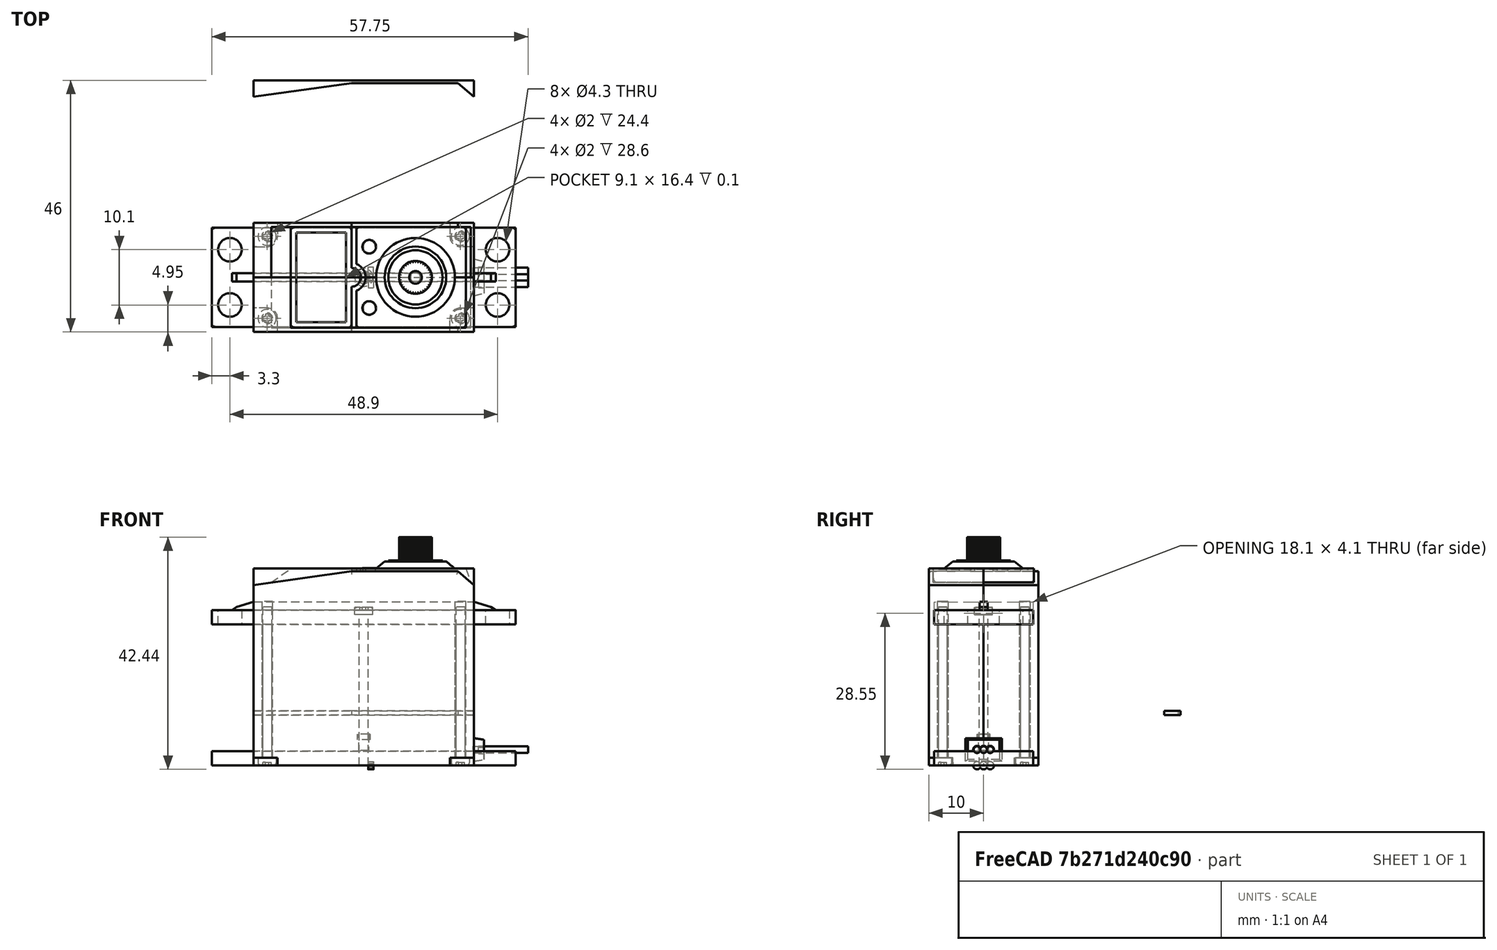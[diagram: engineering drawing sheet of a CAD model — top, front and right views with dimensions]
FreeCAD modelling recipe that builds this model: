
FCSTD DOCUMENT  (FreeCAD 0.14R3702 (Git))
Label: Futaba3003
Comment: It has been modeled using a caliper and a real Futaba 3003 servo
License: CC-BY 3.0
LicenseURL: http://creativecommons.org/licenses/by/3.0/
objects: Sketcher::SketchObject×24, PartDesign::Pocket×12, Part::Feature×10, Part::MultiFuse×7, App::DocumentObjectGroup×6, PartDesign::Pad×5, Part::Loft×3, Part::Cylinder×3, Part::Mirroring×2, Part::Fillet×2, PartDesign::PolarPattern×1, PartDesign::Revolution×1, PartDesign::Fillet×1, PartDesign::Mirrored×1, Part::Cut×1
note: 91 computed .brp shape members not serialized (recipe doc carries the construction recipe); baked Part::Feature solids carry a one-line shape summary decoded from their .brp

FEATURE [Sketcher::SketchObject] Sketch  label="body-sketch"
  Placement = pos=(0,0,0) rot=(1,0,0;1.5708rad)
  sketch-geometry (4):
    g0: LineSegment StartX=-20.15 StartY=36 StartZ=0 EndX=20.15 EndY=36 EndZ=0
    g1: LineSegment StartX=20.15 StartY=0 StartZ=0 EndX=-20.15 EndY=0 EndZ=0
    g2: LineSegment StartX=-20.15 StartY=0 StartZ=0 EndX=-20.15 EndY=36 EndZ=0
    g3: LineSegment StartX=20.15 StartY=36 StartZ=0 EndX=20.15 EndY=0 EndZ=0
  constraints (11):
    c: Coincident(g3,g1)
    c: Coincident(g1,g2)
    c: Horizontal(g0)
    c: Horizontal(g1)
    c: Vertical(g2)
    c: Symmetric(g0,g0,g-2)
    c: PointOnObject(g3,g-1)
    c: DistanceX(g0) = 40.3
    c: DistanceY(g0,g1) = -36
    c: Coincident(g2,g0)
    c: Coincident(g3,g0)
FEATURE [PartDesign::Pad] Pad  label="main_body"
  Length = 10
  Length2 = 100
  Placement = pos=(0,0,0) rot=(1,0,0;1.5708rad)
  Sketch = -> Sketch
  Type = 0
FEATURE [Sketcher::SketchObject] Sketch001  label="lateral-layer1-sketch"
  ExternalGeometry = -> [Pad]
  Placement = pos=(0,-10,0) rot=(1,0,0;1.5708rad)
  Support = -> Pad [Face14]
  sketch-geometry (6):
    g0: LineSegment StartX=20.15 StartY=33 StartZ=0 EndX=17.18 EndY=35.52 EndZ=0
    g1: LineSegment StartX=17.18 StartY=35.52 StartZ=0 EndX=-2.25 EndY=35.52 EndZ=0
    g2: LineSegment StartX=-2.25 StartY=35.52 StartZ=0 EndX=-20.15 EndY=33 EndZ=0
    g3: LineSegment StartX=-20.15 StartY=33 StartZ=0 EndX=-20.15 EndY=36 EndZ=0
    g4: LineSegment StartX=-20.15 StartY=36 StartZ=0 EndX=20.15 EndY=36 EndZ=0
    g5: LineSegment StartX=20.15 StartY=36 StartZ=0 EndX=20.15 EndY=33 EndZ=0
  constraints (16):
    c: Coincident(g0,g1)
    c: Horizontal(g1)
    c: Coincident(g1,g2)
    c: Coincident(g3,g2)
    c: Coincident(g4,g3)
    c: DistanceY(g0) = 33
    c: DistanceY(g4,g0) = -0.48
    c: DistanceX(g0,g0) = -2.97
    c: DistanceX(g4,g1) = -22.4
    c: Coincident(g5,g4)
    c: Coincident(g5,g0)
    c: PointOnObject(g0,g-4)
    c: Coincident(g4,g-4)
    c: Coincident(g3,g-3)
    c: PointOnObject(g2,g-3)
    c: DistanceY(g-1,g2) = 33
FEATURE [Sketcher::SketchObject] Sketch003
  Placement = pos=(0,0,0) rot=(0.57735,0.57735,0.57735;2.0944rad)
  sketch-geometry (4):
    g0: LineSegment StartX=-3.35 StartY=2.1 StartZ=0 EndX=3.35 EndY=2.1 EndZ=0
    g1: LineSegment StartX=3.35 StartY=2.1 StartZ=0 EndX=3.35 EndY=-2.1 EndZ=0
    g2: LineSegment StartX=3.35 StartY=-2.1 StartZ=0 EndX=-3.35 EndY=-2.1 EndZ=0
    g3: LineSegment StartX=-3.35 StartY=-2.1 StartZ=0 EndX=-3.35 EndY=2.1 EndZ=0
  constraints (12):
    c: Coincident(g0,g1)
    c: Coincident(g2,g3)
    c: Coincident(g3,g0)
    c: Horizontal(g0)
    c: Horizontal(g2)
    c: Vertical(g1)
    c: Vertical(g3)
    c: Symmetric(g0,g0,g-2)
    c: Coincident(g1,g2)
    c: DistanceY(g1) = -4.2
    c: DistanceX(g0) = 6.7
    c: Symmetric(g0,g2,g-1)
FEATURE [Sketcher::SketchObject] Sketch004
  Placement = pos=(1.8,0,0) rot=(0.57735,0.57735,0.57735;2.0944rad)
  sketch-geometry (4):
    g0: LineSegment StartX=-2.9 StartY=1.825 StartZ=0 EndX=2.9 EndY=1.825 EndZ=0
    g1: LineSegment StartX=2.9 StartY=1.825 StartZ=0 EndX=2.9 EndY=-1.825 EndZ=0
    g2: LineSegment StartX=2.9 StartY=-1.825 StartZ=0 EndX=-2.9 EndY=-1.825 EndZ=0
    g3: LineSegment StartX=-2.9 StartY=-1.825 StartZ=0 EndX=-2.9 EndY=1.825 EndZ=0
  constraints (12):
    c: Coincident(g0,g1)
    c: Coincident(g2,g3)
    c: Coincident(g3,g0)
    c: Horizontal(g0)
    c: Horizontal(g2)
    c: Vertical(g1)
    c: Vertical(g3)
    c: Symmetric(g0,g0,g-2)
    c: Coincident(g1,g2)
    c: DistanceY(g1) = -3.65
    c: DistanceX(g0) = 5.8
    c: Symmetric(g0,g2,g-1)
FEATURE [Part::Loft] Loft  label="wire-holder-body"
  Closed = false
  Placement = pos=(20.15,0,2.9) rot=(0,0,1;0rad)
  Ruled = false
  Sections = -> [Sketch003,Sketch004]
  Solid = true
FEATURE [Part::Cylinder] Cylinder  label="red-wire"
  Angle = 360
  Height = 10
  Placement = pos=(0,0,0) rot=(0,1,0;1.5708rad)
  Radius = 0.6
FEATURE [Part::Cylinder] Cylinder001  label="white-wire"
  Angle = 360
  Height = 10
  Placement = pos=(0,1.2,0) rot=(0,1,0;1.5708rad)
  Radius = 0.6
FEATURE [Part::Cylinder] Cylinder002  label="blck-wire"
  Angle = 360
  Height = 10
  Placement = pos=(0,-1.2,0) rot=(0,1,0;1.5708rad)
  Radius = 0.6
FEATURE [Sketcher::SketchObject] Sketch005
  ExternalGeometry = -> [Loft]
  Placement = pos=(21.95,0,2.9) rot=(0.57735,0.57735,0.57735;2.0944rad)
  Support = -> Loft [Face6]
  sketch-geometry (6):
    g0: LineSegment [constr] StartX=-1.2 StartY=0 StartZ=0 EndX=1.2 EndY=0 EndZ=0
    g1: ArcOfCircle CenterX=-1.2 CenterY=0 CenterZ=0 NormalX=0 NormalY=0 NormalZ=1 Radius=0.7 StartAngle=0.5411 EndAngle=5.74209
    g2: ArcOfCircle CenterX=0 CenterY=0 CenterZ=0 NormalX=0 NormalY=0 NormalZ=1 Radius=0.7 StartAngle=0.5411 EndAngle=2.60049
    g3: ArcOfCircle CenterX=0 CenterY=0 CenterZ=0 NormalX=0 NormalY=0 NormalZ=1 Radius=0.7 StartAngle=3.68269 EndAngle=5.74209
    g4: ArcOfCircle CenterX=1.2 CenterY=0 CenterZ=0 NormalX=0 NormalY=0 NormalZ=1 Radius=0.7 StartAngle=3.68269 EndAngle=8.88368
    g5: LineSegment [constr] StartX=-1.2 StartY=0 StartZ=0 EndX=-1.2 EndY=-0.7 EndZ=0
  constraints (20):
    c: Horizontal(g0)
    c: Symmetric(g0,g0,g-2)
    c: Coincident(g1,g0)
    c: PointOnObject(g2,g0)
    c: Coincident(g2,g1)
    c: PointOnObject(g2,g-2)
    c: Coincident(g3,g2)
    c: Coincident(g3,g1)
    c: Coincident(g4,g0)
    c: Coincident(g4,g2)
    c: Coincident(g4,g3)
    c: Equal(g1,g2)
    c: Equal(g2,g4)
    c: Equal(g4,g3)
    c: DistanceX(g2,g0) = 1.2
    c: Coincident(g5,g0)
    c: Vertical(g5)
    c: PointOnObject(g5,g1)
    c: Radius(g4) = 0.7
    c: PointOnObject(g0,g-1)
FEATURE [PartDesign::Pocket] Pocket002  label="wire-holder"
  Length = 1
  Placement = pos=(20.15,0,2.9) rot=(0,0,1;0rad)
  Sketch = -> Sketch005
  Type = 0
FEATURE [App::DocumentObjectGroup] Group  label="servo-wire-holder"
  Group = -> [Pocket002,Loft]
FEATURE [PartDesign::Pocket] Pocket  label="lateral-layer1"
  Length = 0.8
  Placement = pos=(0,0,0) rot=(1,0,0;1.5708rad)
  Sketch = -> Sketch001
  Type = 0
FEATURE [Sketcher::SketchObject] Sketch002  label="lateral-layer2-sketch"
  Placement = pos=(0,-9.2,0) rot=(1,0,0;1.5708rad)
  Support = -> Pocket [Face4]
  sketch-geometry (12):
    g0: GeomPoint [constr] X=19.55 Y=33.5091 Z=0
    g1: GeomPoint [constr] X=18.65 Y=36 Z=0
    g2: LineSegment StartX=18.65 StartY=36 StartZ=0 EndX=19.55 EndY=33.5091 EndZ=0
    g3: LineSegment StartX=19.55 StartY=33.5091 StartZ=0 EndX=20.15 EndY=33 EndZ=0
    g4: LineSegment StartX=18.65 StartY=36 StartZ=0 EndX=20.15 EndY=36 EndZ=0
    g5: LineSegment StartX=20.15 StartY=36 StartZ=0 EndX=20.15 EndY=33 EndZ=0
    g6: GeomPoint [constr] X=-16.9 Y=33.4575 Z=0
    g7: GeomPoint [constr] X=-13.35 Y=36 Z=0
    g8: LineSegment StartX=-20.15 StartY=33 StartZ=0 EndX=-16.9 EndY=33.4575 EndZ=0
    g9: LineSegment StartX=-16.9 StartY=33.4575 StartZ=0 EndX=-13.35 EndY=36 EndZ=0
    g10: LineSegment StartX=-20.15 StartY=33 StartZ=0 EndX=-20.15 EndY=36 EndZ=0
    g11: LineSegment StartX=-20.15 StartY=36 StartZ=0 EndX=-13.35 EndY=36 EndZ=0
  constraints (16):
    c: Coincident(g2,g1)
    c: Coincident(g2,g0)
    c: Coincident(g4,g1)
    c: Coincident(g5,g4)
    c: Coincident(g5,g3)
    c: Coincident(g3,g0)
    c: Coincident(g8,g6)
    c: Coincident(g9,g6)
    c: Coincident(g9,g7)
    c: DistanceX(g8,g6) = 3.25
    c: DistanceX(g7,g4) = 33.5
    c: Coincident(g10,g8)
    c: Coincident(g11,g10)
    c: Coincident(g11,g7)
    c: DistanceX(g4,g0) = -0.6
    c: DistanceX(g1,g4) = 1.5
FEATURE [PartDesign::Pocket] Pocket003  label="lateral-layer2"
  Length = 5
  Placement = pos=(0,0,0) rot=(1,0,0;1.5708rad)
  Sketch = -> Sketch002
  Type = 1
FEATURE [Part::Mirroring] Part__Mirroring  label="lateral-layer2 (Mirror #1)"
  Base = (0,0,0)
  Normal = (0,1,0)
  Source = -> Pocket003
FEATURE [Sketcher::SketchObject] Sketch006  label="ear-body-sketch"
  sketch-geometry (4):
    g0: LineSegment StartX=-27.75 StartY=9.05 StartZ=0 EndX=27.75 EndY=9.05 EndZ=0
    g1: LineSegment StartX=27.75 StartY=9.05 StartZ=0 EndX=27.75 EndY=-9.05 EndZ=0
    g2: LineSegment StartX=27.75 StartY=-9.05 StartZ=0 EndX=-27.75 EndY=-9.05 EndZ=0
    g3: LineSegment StartX=-27.75 StartY=-9.05 StartZ=0 EndX=-27.75 EndY=9.05 EndZ=0
  constraints (11):
    c: Coincident(g0,g1)
    c: Coincident(g1,g2)
    c: Coincident(g2,g3)
    c: Coincident(g3,g0)
    c: Horizontal(g0)
    c: Horizontal(g2)
    c: Vertical(g1)
    c: Vertical(g3)
    c: Symmetric(g0,g1,g-1)
    c: DistanceX(g0) = 55.5
    c: DistanceY(g1) = -18.1
FEATURE [PartDesign::Pad] Pad001  label="ear-body"
  Length = 2.6
  Length2 = 100
  Sketch = -> Sketch006
  Type = 0
FEATURE [Sketcher::SketchObject] Sketch007  label="ear-holes-sketch"
  Placement = pos=(0,0,2.6) rot=(0,0,1;0rad)
  Support = -> Pad001 [Face6]
  sketch-geometry (12):
    g0: Circle CenterX=-24.45 CenterY=5.05 CenterZ=0 NormalX=0 NormalY=0 NormalZ=1 Radius=2.15
    g1: Circle CenterX=-24.45 CenterY=-5.05 CenterZ=0 NormalX=0 NormalY=0 NormalZ=1 Radius=2.15
    g2: Circle CenterX=24.45 CenterY=5.05 CenterZ=0 NormalX=0 NormalY=0 NormalZ=1 Radius=2.15
    g3: Circle CenterX=24.45 CenterY=-5.05 CenterZ=0 NormalX=0 NormalY=0 NormalZ=1 Radius=2.15
    g4: LineSegment [constr] StartX=-24.45 StartY=5.05 StartZ=0 EndX=24.45 EndY=5.05 EndZ=0
    g5: LineSegment [constr] StartX=24.45 StartY=5.05 StartZ=0 EndX=24.45 EndY=-5.05 EndZ=0
    g6: LineSegment [constr] StartX=24.45 StartY=-5.05 StartZ=0 EndX=-24.45 EndY=-5.05 EndZ=0
    g7: LineSegment [constr] StartX=-24.45 StartY=-5.05 StartZ=0 EndX=-24.45 EndY=5.05 EndZ=0
    g8: GeomPoint [constr] X=-24.45 Y=2.9 Z=0
    g9: GeomPoint [constr] X=-22.3 Y=5.05 Z=0
    g10: GeomPoint [constr] X=-24.45 Y=-2.9 Z=0
    g11: GeomPoint [constr] X=22.3 Y=5.05 Z=0
  constraints (27):
    c: Coincident(g4,g5)
    c: Coincident(g5,g6)
    c: Coincident(g6,g7)
    c: Coincident(g7,g4)
    c: Horizontal(g4)
    c: Horizontal(g6)
    c: Vertical(g5)
    c: Vertical(g7)
    c: Symmetric(g4,g5,g-1)
    c: Coincident(g2,g4)
    c: Coincident(g3,g5)
    c: Coincident(g1,g6)
    c: Coincident(g0,g4)
    c: PointOnObject(g8,g7)
    c: PointOnObject(g9,g4)
    c: PointOnObject(g8,g0)
    c: PointOnObject(g9,g0)
    c: Equal(g0,g1)
    c: Equal(g1,g2)
    c: Equal(g2,g3)
    c: Radius(g0) = 2.15
    c: PointOnObject(g10,g7)
    c: PointOnObject(g10,g1)
    c: DistanceY(g8,g10) = -5.8
    c: PointOnObject(g11,g4)
    c: PointOnObject(g11,g2)
    c: DistanceX(g9,g11) = 44.6
FEATURE [PartDesign::Pocket] Pocket004  label="ear-holes"
  Length = 5
  Sketch = -> Sketch007
  Type = 1
FEATURE [Sketcher::SketchObject] Sketch008  label="nose-sketch"
  Placement = pos=(0,0,2.6) rot=(1,0,0;1.5708rad)
  sketch-geometry (6):
    g0: LineSegment StartX=-24.1 StartY=0 StartZ=0 EndX=-23.23 EndY=0.6 EndZ=0
    g1: LineSegment StartX=-23.23 StartY=0.6 StartZ=0 EndX=-20.15 EndY=1.5 EndZ=0
    g2: LineSegment StartX=-20.15 StartY=1.5 StartZ=0 EndX=20.15 EndY=1.5 EndZ=0
    g3: LineSegment StartX=20.15 StartY=1.5 StartZ=0 EndX=23.23 EndY=0.6 EndZ=0
    g4: LineSegment StartX=23.23 StartY=0.6 StartZ=0 EndX=24.1 EndY=0 EndZ=0
    g5: LineSegment StartX=24.1 StartY=0 StartZ=0 EndX=-24.1 EndY=0 EndZ=0
  constraints (17):
    c: PointOnObject(g0,g-1)
    c: Coincident(g0,g1)
    c: Coincident(g1,g2)
    c: Horizontal(g2)
    c: Coincident(g2,g3)
    c: Coincident(g3,g4)
    c: PointOnObject(g4,g-1)
    c: Coincident(g4,g5)
    c: Coincident(g5,g0)
    c: DistanceX(g2) = 40.3
    c: Symmetric(g1,g2,g-2)
    c: Symmetric(g3,g0,g-2)
    c: Symmetric(g0,g4,g-2)
    c: DistanceX(g0,g4) = 48.2
    c: DistanceX(g0,g1) = 3.08
    c: DistanceY(g0,g1) = 1.5
    c: DistanceY(g0,g0) = -0.6
FEATURE [PartDesign::Pad] Pad002  label="nose"
  Length = 1.5
  Length2 = 100
  Midplane = true
  Placement = pos=(0,0,2.6) rot=(1,0,0;1.5708rad)
  Sketch = -> Sketch008
  Type = 0
FEATURE [Sketcher::SketchObject] Sketch010
  sketch-geometry (1):
    g0: Circle CenterX=0 CenterY=0 CenterZ=0 NormalX=0 NormalY=0 NormalZ=1 Radius=7.2
  constraints (2):
    c: Coincident(g0,g-1)
    c: Radius(g0) = 7.2
FEATURE [Sketcher::SketchObject] Sketch011
  Placement = pos=(0,0,1.3) rot=(0,0,1;0rad)
  sketch-geometry (1):
    g0: Circle CenterX=0 CenterY=0 CenterZ=0 NormalX=0 NormalY=0 NormalZ=1 Radius=5.625
  constraints (2):
    c: Coincident(g0,g-1)
    c: Radius(g0) = 5.625
FEATURE [Part::Loft] Loft001  label="shaft-base1"
  Closed = false
  Placement = pos=(9.45,0,36) rot=(0,0,1;0rad)
  Ruled = false
  Sections = -> [Sketch010,Sketch011]
  Solid = true
FEATURE [Sketcher::SketchObject] Sketch012
  Placement = pos=(9.45,0,37.3) rot=(0,0,1;0rad)
  Support = -> Loft001 [Face3]
  sketch-geometry (1):
    g0: Circle CenterX=0 CenterY=0 CenterZ=0 NormalX=0 NormalY=0 NormalZ=1 Radius=4.95
  constraints (2):
    c: Coincident(g0,g-1)
    c: Radius(g0) = 4.95
FEATURE [PartDesign::Pad] Pad005  label="shaft-base2"
  Length = 0.2
  Length2 = 100
  Placement = pos=(9.45,0,36) rot=(0,0,1;0rad)
  Sketch = -> Sketch012
  Type = 0
FEATURE [Sketcher::SketchObject] Sketch013
  Placement = pos=(9.45,0,37.5) rot=(0,0,1;0rad)
  Support = -> Pad005 [Face5]
  sketch-geometry (1):
    g0: Circle CenterX=0 CenterY=0 CenterZ=0 NormalX=0 NormalY=0 NormalZ=1 Radius=3
  constraints (2):
    c: Coincident(g0,g-1)
    c: Radius(g0) = 3
FEATURE [PartDesign::Pad] Pad006  label="base-plus-basic-shaft"
  Length = 4.24
  Length2 = 100
  Placement = pos=(9.45,0,36) rot=(0,0,1;0rad)
  Sketch = -> Sketch013
  Type = 0
FEATURE [Sketcher::SketchObject] Sketch014  label="master-tooth-sketch"
  ExternalGeometry = -> [Pad006]
  Placement = pos=(9.45,0,41.74) rot=(0,0,1;0rad)
  Support = -> Pad006 [Face7]
  sketch-geometry (8):
    g0: Circle [constr] CenterX=0 CenterY=0 CenterZ=0 NormalX=0 NormalY=0 NormalZ=1 Radius=3.2
    g1: Circle [constr] CenterX=0 CenterY=0 CenterZ=0 NormalX=0 NormalY=0 NormalZ=1 Radius=2.8
    g2: LineSegment StartX=-0.1 StartY=3.19844 StartZ=0 EndX=0.1 EndY=3.19844 EndZ=0
    g3: LineSegment [constr] StartX=-0.1 StartY=3.19844 StartZ=0 EndX=0 EndY=0 EndZ=0
    g4: LineSegment [constr] StartX=0.1 StartY=3.19844 StartZ=0 EndX=0 EndY=0 EndZ=0
    g5: LineSegment StartX=-0.1 StartY=3.19844 StartZ=0 EndX=-0.0875 EndY=2.79863 EndZ=0
    g6: LineSegment StartX=-0.0875 StartY=2.79863 StartZ=0 EndX=0.0875 EndY=2.79863 EndZ=0
    g7: LineSegment StartX=0.0875 StartY=2.79863 StartZ=0 EndX=0.1 EndY=3.19844 EndZ=0
  constraints (20):
    c: Coincident(g0,g-1)
    c: Radius(g0) = 3.2
    c: Coincident(g1,g-1)
    c: Radius(g1) = 2.8
    c: Horizontal(g2)
    c: PointOnObject(g2,g0)
    c: PointOnObject(g2,g0)
    c: DistanceX(g2,g2) = 0.2
    c: Coincident(g3,g2)
    c: Coincident(g2,g4)
    c: Coincident(g4,g-1)
    c: Coincident(g3,g-1)
    c: Coincident(g5,g6)
    c: Coincident(g6,g7)
    c: Coincident(g5,g2)
    c: Coincident(g7,g2)
    c: PointOnObject(g5,g3)
    c: PointOnObject(g6,g4)
    c: PointOnObject(g5,g1)
    c: PointOnObject(g6,g1)
FEATURE [PartDesign::Pocket] Pocket005  label="master-tooth"
  Length = 4.1
  Placement = pos=(9.45,0,36) rot=(0,0,1;0rad)
  Sketch = -> Sketch014
  Type = 0
FEATURE [PartDesign::PolarPattern] PolarPattern  label="shaft-teeth"
  Angle = 360
  Axis = -> Sketch014 [N_Axis]
  Occurrences = 36
  Originals = -> [Pocket005]
  Placement = pos=(9.45,0,36) rot=(0,0,1;0rad)
FEATURE [Sketcher::SketchObject] Sketch017  label="top-cone-top"
  sketch-geometry (1):
    g0: Circle CenterX=0 CenterY=0 CenterZ=0 NormalX=0 NormalY=0 NormalZ=1 Radius=1.1
  constraints (2):
    c: Coincident(g0,g-1)
    c: Radius(g0) = 1.1
FEATURE [Sketcher::SketchObject] Sketch018  label="top-cone-bottom"
  Placement = pos=(0,0,0.6) rot=(0,0,1;0rad)
  sketch-geometry (1):
    g0: Circle CenterX=0 CenterY=0 CenterZ=0 NormalX=0 NormalY=0 NormalZ=1 Radius=1.25
  constraints (2):
    c: Coincident(g0,g-1)
    c: Radius(g0) = 1.25
FEATURE [Sketcher::SketchObject] Sketch021
  Placement = pos=(0,0,0) rot=(1,0,0;1.5708rad)
  sketch-geometry (6):
    g0: LineSegment StartX=0 StartY=0 StartZ=0 EndX=0.81 EndY=0 EndZ=0
    g1: LineSegment StartX=0.81 StartY=0 StartZ=0 EndX=0.81 EndY=27.6 EndZ=0
    g2: LineSegment StartX=0 StartY=28.9 StartZ=0 EndX=0 EndY=0 EndZ=0
    g3: LineSegment StartX=0.81 StartY=27.6 StartZ=0 EndX=1.65 EndY=27.6 EndZ=0
    g4: LineSegment StartX=1.65 StartY=27.6 StartZ=0 EndX=1.65 EndY=28.9 EndZ=0
    g5: LineSegment StartX=1.65 StartY=28.9 StartZ=0 EndX=0 EndY=28.9 EndZ=0
  constraints (17):
    c: Coincident(g0,g1)
    c: Coincident(g2,g0)
    c: Horizontal(g0)
    c: Vertical(g1)
    c: Vertical(g2)
    c: Coincident(g0,g-1)
    c: Coincident(g3,g4)
    c: Coincident(g4,g5)
    c: Coincident(g2,g5)
    c: Horizontal(g5)
    c: Coincident(g3,g1)
    c: Horizontal(g3)
    c: Vertical(g4)
    c: DistanceY(g2) = -28.9
    c: DistanceX(g0) = 0.81
    c: DistanceX(g5) = -1.65
    c: DistanceY(g4) = 1.3
FEATURE [PartDesign::Revolution] Revolution  label="screw-shape"
  Angle = 360
  Axis = (0,0,1)
  Base = (0,0,0)
  Placement = pos=(0,0,0) rot=(1,0,0;1.5708rad)
  ReferenceAxis = -> Sketch021 [V_Axis]
  Reversed = true
  Sketch = -> Sketch021
FEATURE [Sketcher::SketchObject] Sketch022  label="screw-cross-sketch"
  Placement = pos=(0,0,28.9) rot=(0,0,1;3.14159rad)
  Support = -> Revolution [Face5]
  sketch-geometry (12):
    g0: LineSegment StartX=-0.3 StartY=0.75 StartZ=0 EndX=0.3 EndY=0.75 EndZ=0
    g1: LineSegment StartX=0.3 StartY=0.75 StartZ=0 EndX=0.3 EndY=0.3 EndZ=0
    g2: LineSegment StartX=0.3 StartY=-0.75 StartZ=0 EndX=-0.3 EndY=-0.75 EndZ=0
    g3: LineSegment StartX=-0.3 StartY=-0.75 StartZ=0 EndX=-0.3 EndY=-0.3 EndZ=0
    g4: LineSegment StartX=-0.75 StartY=0.3 StartZ=0 EndX=-0.3 EndY=0.3 EndZ=0
    g5: LineSegment StartX=0.75 StartY=0.3 StartZ=0 EndX=0.75 EndY=-0.3 EndZ=0
    g6: LineSegment StartX=0.75 StartY=-0.3 StartZ=0 EndX=0.3 EndY=-0.3 EndZ=0
    g7: LineSegment StartX=-0.75 StartY=-0.3 StartZ=0 EndX=-0.75 EndY=0.3 EndZ=0
    g8: LineSegment StartX=-0.3 StartY=0.3 StartZ=0 EndX=-0.3 EndY=0.75 EndZ=0
    g9: LineSegment StartX=0.3 StartY=-0.3 StartZ=0 EndX=0.3 EndY=-0.75 EndZ=0
    g10: LineSegment StartX=0.3 StartY=0.3 StartZ=0 EndX=0.75 EndY=0.3 EndZ=0
    g11: LineSegment StartX=-0.3 StartY=-0.3 StartZ=0 EndX=-0.75 EndY=-0.3 EndZ=0
  constraints (30):
    c: Coincident(g0,g1)
    c: Coincident(g9,g2)
    c: Coincident(g2,g3)
    c: Coincident(g8,g0)
    c: Horizontal(g0)
    c: Horizontal(g2)
    c: Vertical(g1)
    c: Vertical(g3)
    c: Symmetric(g0,g9,g-1)
    c: Coincident(g10,g5)
    c: Coincident(g5,g6)
    c: Coincident(g11,g7)
    c: Coincident(g7,g4)
    c: Horizontal(g4)
    c: Horizontal(g6)
    c: Vertical(g5)
    c: Vertical(g7)
    c: Symmetric(g4,g5,g-1)
    c: Tangent(g3,g8)
    c: Tangent(g1,g9)
    c: Coincident(g4,g8)
    c: Coincident(g10,g1)
    c: Tangent(g4,g10)
    c: Coincident(g6,g9)
    c: Coincident(g11,g3)
    c: Tangent(g6,g11)
    c: Equal(g0,g7)
    c: Equal(g8,g4)
    c: DistanceX(g4,g5) = 1.5
    c: DistanceX(g0) = 0.6
FEATURE [PartDesign::Pocket] Pocket002006
  Length = 0.5
  Placement = pos=(0,0,0) rot=(1,0,0;1.5708rad)
  Sketch = -> Sketch022
  Type = 0
FEATURE [PartDesign::Fillet] Fillet  label="servo-screw-final1"
  Base = -> Pocket002006 [Edge5]
  Placement = pos=(0,0,0) rot=(1,0,0;1.5708rad)
  Radius = 0.4
FEATURE [Part::Feature] Fillet001  label="servo-screw1"
  Placement = pos=(17.6429,-7.49289,29) rot=(-1,0,0;1.5708rad)
  shape: bbox 3.572 x 3.572 x 28.9 mm, 19 faces (baked)
FEATURE [Part::Feature] Fillet001001  label="servo-screw002"
  Placement = pos=(-17.6429,-7.49289,29) rot=(-1,0,0;1.5708rad)
  shape: bbox 3.572 x 3.572 x 28.9 mm, 19 faces (baked)
FEATURE [Part::Feature] Fillet001002  label="servo-screw003"
  Placement = pos=(-17.6429,7.49289,29) rot=(-1,0,0;1.5708rad)
  shape: bbox 3.572 x 3.572 x 28.9 mm, 19 faces (baked)
FEATURE [Part::Feature] Fillet001003  label="servo-screw004"
  Placement = pos=(17.6429,7.49289,29) rot=(-1,0,0;1.5708rad)
  shape: bbox 3.572 x 3.572 x 28.9 mm, 19 faces (baked)
FEATURE [Sketcher::SketchObject] Sketch023
  Placement = pos=(9.45,0,41.74) rot=(0,0,1;0rad)
  Support = -> PolarPattern [Face9]
  sketch-geometry (1):
    g0: Circle CenterX=0 CenterY=0 CenterZ=0 NormalX=0 NormalY=0 NormalZ=1 Radius=0.9
  constraints (2):
    c: Coincident(g0,g-1)
    c: Radius(g0) = 0.9
FEATURE [PartDesign::Pocket] Pocket002007  label="shaft-drill-1"
  Length = 3
  Placement = pos=(9.45,0,36) rot=(0,0,1;0rad)
  Sketch = -> Sketch023
  Type = 0
FEATURE [Sketcher::SketchObject] Sketch024
  Placement = pos=(9.45,0,41.74) rot=(0,0,1;0rad)
  Support = -> Pocket002007 [Face9]
  sketch-geometry (1):
    g0: Circle CenterX=0 CenterY=0 CenterZ=0 NormalX=0 NormalY=0 NormalZ=1 Radius=1.15
  constraints (2):
    c: Coincident(g0,g-1)
    c: Radius(g0) = 1.15
FEATURE [PartDesign::Pocket] Pocket002008  label="shaft-drill-2"
  Length = 1
  Placement = pos=(9.45,0,36) rot=(0,0,1;0rad)
  Sketch = -> Sketch024
  Type = 0
FEATURE [App::DocumentObjectGroup] Group002  label="servo-shaft"
  Group = -> [Loft001,Pad005,Pad006,Pocket005,PolarPattern,Pocket002007,Pocket002008]
FEATURE [Part::Loft] Loft002  label="top-cone-master"
  Closed = false
  Placement = pos=(1,5.6,35.5) rot=(0,0,1;0rad)
  Ruled = false
  Sections = -> [Sketch017,Sketch018]
  Solid = true
FEATURE [Part::MultiFuse] Fusion006  label="servo-body001"
  Shapes = -> [Pocket003,Part__Mirroring]
FEATURE [Sketcher::SketchObject] Sketch015  label="top-details-1-sketch"
  ExternalGeometry = -> [Fusion006]
  Placement = pos=(0,0,36) rot=(0,0,1;0rad)
  Support = -> Fusion006 [Face8]
  sketch-geometry (10):
    g0: ArcOfCircle CenterX=-2.25 CenterY=0 CenterZ=0 NormalX=0 NormalY=0 NormalZ=1 Radius=1.7 StartAngle=4.71239 EndAngle=7.85398
    g1: LineSegment StartX=-2.25 StartY=9.2 StartZ=0 EndX=-2.25 EndY=1.7 EndZ=0
    g2: LineSegment StartX=-2.25 StartY=-1.7 StartZ=0 EndX=-2.25 EndY=-9.2 EndZ=0
    g3: ArcOfCircle CenterX=-2.25 CenterY=0 CenterZ=0 NormalX=0 NormalY=0 NormalZ=1 Radius=2.6 StartAngle=5.06586 EndAngle=7.50051
    g4: LineSegment [constr] StartX=-0.55 StartY=0 StartZ=0 EndX=0.35 EndY=0 EndZ=0
    g5: LineSegment [constr] StartX=-1.35 StartY=2.43926 StartZ=0 EndX=-2.25 EndY=2.43926 EndZ=0
    g6: LineSegment StartX=-1.35 StartY=2.43926 StartZ=0 EndX=-1.35 EndY=9.2 EndZ=0
    g7: LineSegment StartX=-2.25 StartY=9.2 StartZ=0 EndX=-1.35 EndY=9.2 EndZ=0
    g8: LineSegment StartX=-1.35 StartY=-2.43926 StartZ=0 EndX=-1.35 EndY=-9.2 EndZ=0
    g9: LineSegment StartX=-2.25 StartY=-9.2 StartZ=0 EndX=-1.35 EndY=-9.2 EndZ=0
  constraints (30):
    c: Radius(g0) = 1.7
    c: Symmetric(g0,g0,g-1)
    c: Coincident(g1,g0)
    c: Vertical(g1)
    c: Vertical(g2)
    c: Coincident(g2,g0)
    c: PointOnObject(g0,g1)
    c: Symmetric(g3,g3,g-1)
    c: PointOnObject(g4,g-1)
    c: Horizontal(g4)
    c: PointOnObject(g4,g0)
    c: PointOnObject(g4,g3)
    c: Coincident(g3,g0)
    c: DistanceX(g4) = 0.9
    c: Horizontal(g5)
    c: PointOnObject(g5,g1)
    c: Vertical(g6)
    c: Horizontal(g7)
    c: Coincident(g7,g1)
    c: Coincident(g7,g6)
    c: Coincident(g6,g3)
    c: DistanceX(g5) = -0.9
    c: Coincident(g5,g3)
    c: Coincident(g8,g3)
    c: Vertical(g8)
    c: Coincident(g9,g2)
    c: Horizontal(g9)
    c: Coincident(g9,g8)
    c: Symmetric(g1,g2,g-1)
    c: Coincident(g1,g-3)
FEATURE [PartDesign::Pocket] Pocket002008004  label="top-details-1"
  Length = 0.48
  Sketch = -> Sketch015
  Type = 0
FEATURE [Sketcher::SketchObject] Sketch016  label="top-details-2-sketch"
  ExternalGeometry = -> [Pocket002008004]
  Placement = pos=(0,0,36) rot=(0,0,1;0rad)
  Support = -> Pocket002008004 [Face21]
  sketch-geometry (6):
    g0: LineSegment StartX=-12.35 StartY=8.2 StartZ=0 EndX=-3.25 EndY=8.2 EndZ=0
    g1: LineSegment StartX=-3.25 StartY=8.2 StartZ=0 EndX=-3.25 EndY=-8.2 EndZ=0
    g2: LineSegment StartX=-3.25 StartY=-8.2 StartZ=0 EndX=-12.35 EndY=-8.2 EndZ=0
    g3: LineSegment StartX=-12.35 StartY=-8.2 StartZ=0 EndX=-12.35 EndY=8.2 EndZ=0
    g4: LineSegment [constr] StartX=-13.35 StartY=9.2 StartZ=0 EndX=-12.35 EndY=8.2 EndZ=0
    g5: LineSegment [constr] StartX=-2.25 StartY=-9.2 StartZ=0 EndX=-3.25 EndY=-8.2 EndZ=0
  constraints (16):
    c: Coincident(g4,g0)
    c: Coincident(g0,g3)
    c: Horizontal(g0)
    c: Vertical(g3)
    c: Coincident(g0,g1)
    c: Vertical(g1)
    c: Coincident(g2,g3)
    c: Horizontal(g2)
    c: Coincident(g1,g2)
    c: Coincident(g5,g1)
    c: DistanceX(g0,g4) = -1
    c: DistanceX(g5,g1) = -1
    c: Coincident(g4,g-3)
    c: Angle(g-3,g4) = 0.785398
    c: Coincident(g5,g-4)
    c: Angle(g5,g-1) = 0.785398
FEATURE [PartDesign::Pocket] Pocket002008007002  label="top-details-2"
  Length = 0.1
  Sketch = -> Sketch016
  Type = 0
FEATURE [Sketcher::SketchObject] Sketch025  label="bottom-details-1-sketch"
  ExternalGeometry = -> [Pocket002008007002]
  Placement = pos=(0,0,0) rot=(1,0,0;3.14159rad)
  Support = -> Pocket002008007002 [Face17]
  sketch-geometry (12):
    g0: LineSegment StartX=-17.6429 StartY=5.6 StartZ=0 EndX=-20.15 EndY=5.6 EndZ=0
    g1: LineSegment StartX=-20.15 StartY=5.6 StartZ=0 EndX=-20.15 EndY=10 EndZ=0
    g2: LineSegment StartX=-15.75 StartY=10 StartZ=0 EndX=-15.75 EndY=7.49289 EndZ=0
    g3: ArcOfCircle CenterX=-17.6429 CenterY=7.49289 CenterZ=0 NormalX=0 NormalY=0 NormalZ=1 Radius=1.89289 StartAngle=4.7124 EndAngle=6.28319
    g4: Circle [constr] CenterX=-17.6429 CenterY=7.49289 CenterZ=0 NormalX=0 NormalY=0 NormalZ=1 Radius=1
    g5: LineSegment StartX=-20.15 StartY=10 StartZ=0 EndX=-15.75 EndY=10 EndZ=0
    g6: LineSegment [constr] StartX=-20.15 StartY=10 StartZ=0 EndX=-18.35 EndY=8.2 EndZ=0
    g7: LineSegment StartX=-20.15 StartY=-5.6 StartZ=0 EndX=-20.15 EndY=-10 EndZ=0
    g8: LineSegment StartX=-20.15 StartY=-5.6 StartZ=0 EndX=-17.6429 EndY=-5.6 EndZ=0
    g9: LineSegment StartX=-20.15 StartY=-10 StartZ=0 EndX=-15.75 EndY=-10 EndZ=0
    g10: LineSegment StartX=-15.75 StartY=-10 StartZ=0 EndX=-15.75 EndY=-7.49289 EndZ=0
    g11: ArcOfCircle CenterX=-17.6429 CenterY=-7.49289 CenterZ=0 NormalX=0 NormalY=0 NormalZ=1 Radius=1.89289 StartAngle=6.28318 EndAngle=7.85397
  constraints (34):
    c: Coincident(g0,g1)
    c: Vertical(g2)
    c: Horizontal(g0)
    c: Vertical(g1)
    c: Coincident(g3,g2)
    c: Coincident(g3,g0)
    c: Tangent(g3,g0)
    c: Radius(g4) = 1
    c: Coincident(g3,g4)
    c: Coincident(g5,g1)
    c: Coincident(g5,g2)
    c: Horizontal(g5)
    c: Coincident(g6,g1)
    c: Angle(g6,g5) = 0.785398
    c: PointOnObject(g6,g4)
    c: PointOnObject(g3,g6)
    c: DistanceX(g5) = 4.4
    c: DistanceX(g6,g1) = -1.8
    c: Coincident(g1,g-3)
    c: Tangent(g2,g3)
    c: Vertical(g7)
    c: Symmetric(g7,g1,g-1)
    c: Symmetric(g7,g0,g-1)
    c: Horizontal(g8)
    c: Coincident(g8,g7)
    c: Symmetric(g8,g0,g-1)
    c: Horizontal(g9)
    c: Coincident(g9,g7)
    c: Symmetric(g9,g2,g-1)
    c: Coincident(g10,g9)
    c: Symmetric(g10,g2,g-1)
    c: Coincident(g11,g8)
    c: Coincident(g11,g10)
    c: Symmetric(g11,g3,g-1)
FEATURE [PartDesign::Pocket] Pocket002008007003  label="bottom-details-1"
  Length = 1.4
  Sketch = -> Sketch025
  Type = 0
FEATURE [PartDesign::Mirrored] Mirrored  label="bottom-details-1-complete"
  MirrorPlane = -> Sketch025 [V_Axis]
  Originals = -> [Pocket002008007003]
FEATURE [Sketcher::SketchObject] Sketch026  label="bottom-drills-sketch"
  ExternalGeometry = -> [Mirrored]
  Placement = pos=(0,0,0) rot=(1,0,0;3.14159rad)
  Support = -> Mirrored [Face19]
  sketch-geometry (6):
    g0: Circle CenterX=-17.6429 CenterY=7.49289 CenterZ=0 NormalX=0 NormalY=0 NormalZ=1 Radius=1
    g1: LineSegment [constr] StartX=-20.15 StartY=10 StartZ=0 EndX=-18.35 EndY=8.2 EndZ=0
    g2: LineSegment [constr] StartX=-20.15 StartY=10 StartZ=0 EndX=0 EndY=10 EndZ=0
    g3: Circle CenterX=-17.6429 CenterY=-7.49289 CenterZ=0 NormalX=0 NormalY=0 NormalZ=1 Radius=1
    g4: Circle CenterX=17.6429 CenterY=7.49289 CenterZ=0 NormalX=0 NormalY=0 NormalZ=1 Radius=1
    g5: Circle CenterX=17.6429 CenterY=-7.49289 CenterZ=0 NormalX=0 NormalY=0 NormalZ=1 Radius=1
  constraints (15):
    c: Radius(g0) = 1
    c: Coincident(g2,g1)
    c: Horizontal(g2)
    c: PointOnObject(g2,g-2)
    c: Angle(g1,g2) = 0.785398
    c: PointOnObject(g1,g0)
    c: PointOnObject(g0,g1)
    c: Coincident(g1,g-3)
    c: DistanceX(g1,g1) = -1.8
    c: Equal(g0,g3)
    c: Equal(g3,g5)
    c: Equal(g5,g4)
    c: Symmetric(g0,g3,g-1)
    c: Symmetric(g0,g4,g-2)
    c: Symmetric(g0,g5,g-1)
FEATURE [PartDesign::Pocket] Pocket002008007004  label="servo-body-final-1"
  Length = 30
  Sketch = -> Sketch026
  Type = 0
FEATURE [Part::Fillet] Fillet001007  label="servo-body-final-rounded"
  Base = -> Pocket002008007004
  Edges = 24 edges r=0.6: [Edge2,Edge5,Edge18,Edge24,Edge25,Edge26,Edge29,Edge30,Edge32,Edge33,Edge36,Edge39,Edge40,Edge41,Edge43,Edge46,Edge52,Edge53,Edge56,Edge59,Edge62,Edge77,Edge93,Edge95]
FEATURE [App::DocumentObjectGroup] Group005  label="servo-body"
  Group = -> [Pad,Pocket,Fusion006,Pocket002008004,Pocket002008007002,Pocket002008007003,Mirrored,Pocket002008007004,Fillet001007]
FEATURE [Part::MultiFuse] Fusion001  label="ears-final"
  Placement = pos=(0,0,25.8) rot=(0,0,1;0rad)
  Shapes = -> [Pocket004,Pad002]
FEATURE [Part::Fillet] Fillet001008  label="ears-final-rounded"
  Base = -> Fusion001
  Edges = 4 edges r=0.6: [Edge1,Edge2,Edge5,Edge8]
FEATURE [App::DocumentObjectGroup] Group001  label="servo-ears"
  Group = -> [Pad001,Pocket004,Pad002,Fusion001,Fillet001008]
FEATURE [Part::Feature] Fillet001007001  label="servo-body-1"
  shape: bbox 40.3 x 20 x 36.49 mm, 79 faces (baked)
FEATURE [Part::Mirroring] Part__Mirroring001  label="cone-2"
  Base = (0,0,0)
  Normal = (0,1,0)
  Source = -> Loft002
FEATURE [Part::MultiFuse] Fusion  label="two-top-cones"
  Shapes = -> [Loft002,Part__Mirroring001]
FEATURE [App::DocumentObjectGroup] Group006  label="top-cone"
  Group = -> [Loft002,Part__Mirroring001,Fusion]
FEATURE [Part::Feature] Fusion007  label="two-top-cones-1"
  shape: bbox 2.5 x 13.7 x 0.6 mm, 6 faces, 2 solids (baked)
FEATURE [Part::Cut] Cut  label="servo-body-2"
  Base = -> Fillet001007001
  Tool = -> Fusion007
FEATURE [Part::Feature] Pocket002008007005  label="servo-shaft-1"
  Placement = pos=(9.45,0,36) rot=(0,0,1;0rad)
  shape: bbox 14.4 x 14.4 x 5.74 mm, 155 faces (baked)
FEATURE [Part::Feature] Fillet001008001  label="servo-ears-1"
  shape: bbox 55.5 x 18.1 x 4.1 mm, 21 faces (baked)
FEATURE [Part::Feature] Pocket002008007006  label="Servo-wire-holder-1"
  Placement = pos=(20.15,0,2.9) rot=(0,0,1;0rad)
  shape: bbox 1.8 x 6.7 x 4.2 mm, 11 faces (baked)
FEATURE [Part::MultiFuse] Fusion008  label="Servo-no-screws"
  Shapes = -> [Cut,Fillet001008001,Pocket002008007006,Pocket002008007005]
FEATURE [Part::MultiFuse] Fusion009  label="servo-screws"
  Shapes = -> [Fillet001,Fillet001001,Fillet001002,Fillet001003]
FEATURE [App::DocumentObjectGroup] Group004  label="Servo-bottom-screws"
  Group = -> [Revolution,Pocket002006,Fillet,Fillet001,Fillet001001,Fillet001002,Fillet001003,Fusion009]
FEATURE [Part::Feature] Fusion009001  label="servo-screws-four"
  shape: bbox 38.86 x 18.56 x 28.9 mm, 76 faces, 4 solids (baked)
FEATURE [Part::MultiFuse] Fusion009002  label="Servo-Futaba3003-final"
  Shapes = -> [Fusion008,Fusion009001]
FEATURE [Part::MultiFuse] Fusion009003  label="servo-wires"
  Placement = pos=(20,0,2.9) rot=(0,0,1;0rad)
  Shapes = -> [Cylinder,Cylinder002,Cylinder001]
